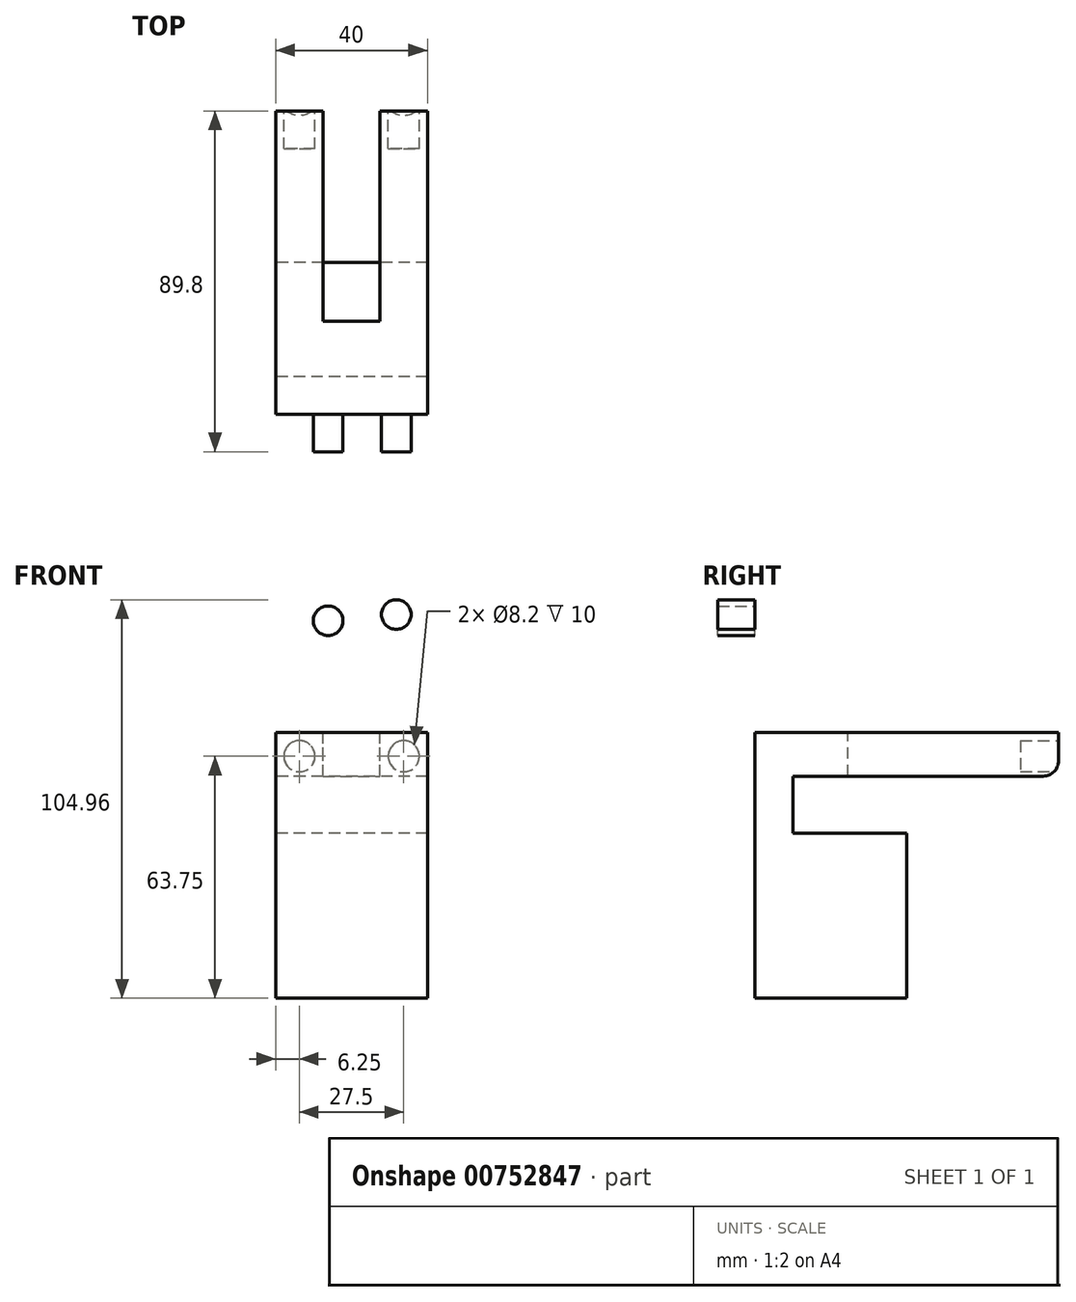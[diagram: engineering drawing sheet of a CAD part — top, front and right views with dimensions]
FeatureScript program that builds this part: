
annotation { "Feature Type Name" : "Feature", "Feature Type Description" : "" }
export const myFeature = defineFeature(function(context is Context, id is Id, definition is map)
    precondition{}
    {
        {
            var Q0;
            Q0=qCreatedBy(makeId("Right.planeOp"),FACE);
            var sketch = newSketch(context, id + "F0", { "sketchPlane" : qUnion([Q0])});
            skLineSegment(sketch, "E0.bottom", {"start": v(0, 0) * mm, "end": v(80, 0) * mm});
            skLineSegment(sketch, "E0.top", {"start": v(0, -40) * mm, "end": v(80, -40) * mm});
            skLineSegment(sketch, "E0.left", {"start": v(0, 0) * mm, "end": v(0, -40) * mm});
            skLineSegment(sketch, "E0.right", {"start": v(80, 0) * mm, "end": v(80, -7.5) * mm});
            skLineSegment(sketch, "E1.bottom", {"start": v(10, -11.5) * mm, "end": v(76, -11.5) * mm});
            skLineSegment(sketch, "E1.top", {"start": v(10, -26.5) * mm, "end": v(80, -26.5) * mm});
            skLineSegment(sketch, "E1.left", {"start": v(10, -11.5) * mm, "end": v(10, -26.5) * mm});
            skLineSegment(sketch, "E1.right", {"start": v(80, -12.5) * mm, "end": v(80, -26.5) * mm});
            skLineSegment(sketch, "E2", {"start": v(40, -40) * mm, "end": v(40, -26.5) * mm});
            skPoint(sketch, "E3.newPointB", {"position": v(80, -40) * mm});
            skArc(sketch, "E3.filletArc", {"start": v(76, -11.5) * mm, "mid": v(78.83, -10.33) * mm, "end": v(80, -7.5) * mm});
            skSolve(sketch);
        }
        {
            var Q0;
            {var subQ1=sQuery(id+"F0.wireOp",EDGE,"E0.bottom");Q0=makeQuery(id+"F0.imprint","IMPRINT",FACE,{"disambiguationData":[TD([[makeQuery(id+"F0.imprint","IMPRINT",EDGE,{"derivedFrom":subQ1}),-1.0]])]});}
            extrude(context, id + "F1", {"entities" : qUnion([Q0]), "depth" : 40 * mm, "offsetDistance" : 25 * mm});
        }
        {
            var Q0;
            Q0=makeQuery(id+"F1.opExtrude","SWEPT_FACE",FACE,{"disambiguationData":[OSD([sQuery(id+"F0.wireOp",EDGE,"E0.bottom")])]});
            var sketch = newSketch(context, id + "F2", { "sketchPlane" : qUnion([Q0])});
            skCircle(sketch, "E4.cCircle", {"center": v(20, 54.76) * mm, "radius": 6.5 * mm, "construction": true});
            skLineSegment(sketch, "E4.0", {"start": v(24, 48.4) * mm, "end": v(16.5, 48.12) * mm});
            skLineSegment(sketch, "E4.1", {"start": v(16.5, 48.12) * mm, "end": v(12.5, 54.47) * mm});
            skLineSegment(sketch, "E4.2", {"start": v(12.5, 54.47) * mm, "end": v(16, 61.1) * mm});
            skLineSegment(sketch, "E4.3", {"start": v(16, 61.1) * mm, "end": v(23.5, 61.4) * mm});
            skLineSegment(sketch, "E4.4", {"start": v(23.5, 61.4) * mm, "end": v(27.5, 55.04) * mm});
            skLineSegment(sketch, "E4.5", {"start": v(27.5, 55.04) * mm, "end": v(24, 48.4) * mm});
            skPoint(sketch, "E4.0.midPoint", {"position": v(20.25, 48.26) * mm});
            skPoint(sketch, "E5.endSnap0", {"position": v(27.96, 47.74) * mm});
            skLineSegment(sketch, "E6", {"start": v(12.5, 24.53) * mm, "end": v(27.5, 24.53) * mm});
            skLineSegment(sketch, "E7", {"start": v(12.5, 54.47) * mm, "end": v(12.5, 24.53) * mm});
            skLineSegment(sketch, "E8", {"start": v(27.5, 55.04) * mm, "end": v(27.5, 24.53) * mm});
            skLineSegment(sketch, "E9", {"start": v(12.5, 54.47) * mm, "end": v(12.5, 80) * mm});
            skLineSegment(sketch, "E10", {"start": v(27.5, 55.04) * mm, "end": v(27.5, 80) * mm});
            skLineSegment(sketch, "E11", {"start": v(40, 80) * mm, "end": v(40, 0) * mm});
            skSolve(sketch);
        }
        {
            var Q0;
            Q0=makeQuery(id+"F2.imprint","IMPRINT",FACE,{"disambiguationData":[TD([[makeQuery(id+"F2.imprint","IMPRINT",EDGE,{"derivedFrom":sQuery(id+"F2.wireOp",EDGE,"E4.2")}),1.0]])]});
            var Q1;
            Q1=makeQuery(id+"F2.imprint","IMPRINT",FACE,{"disambiguationData":[TD([[makeQuery(id+"F2.imprint","IMPRINT",EDGE,{"derivedFrom":sQuery(id+"F2.wireOp",EDGE,"E4.0")}),-1.0]])]});
            var Q2;
            Q2=makeQuery(id+"F2.imprint","IMPRINT",FACE,{"disambiguationData":[TD([[makeQuery(id+"F2.imprint","IMPRINT",EDGE,{"derivedFrom":sQuery(id+"F2.wireOp",EDGE,"E4.0")}),1.0]])]});
            extrude(context, id + "F3", {"entities" : qUnion([Q0, Q1, Q2]), "operationType" : NewBodyOperationType.REMOVE, "oppositeDirection" : true, "depth" : 13 * mm, "offsetDistance" : 25 * mm});
        }
        {
            var Q0;
            Q0=makeQuery(id+"F1.opExtrude","SWEPT_FACE",FACE,{"disambiguationData":[OSD([sQuery(id+"F0.wireOp",EDGE,"E0.top")])]});
            extrude(context, id + "F4", {"entities" : qUnion([Q0]), "operationType" : NewBodyOperationType.ADD, "depth" : 30 * mm, "offsetDistance" : 25 * mm});
        }
        {
            var Q0;
            {var subQ2=sQuery(id+"F0.wireOp",EDGE,"E0.right");Q0=makeQuery(id+"F3.boolean.opBoolean","SPLIT",FACE,{"disambiguationData":[TD([makeQuery(id+"F3.opExtrude","SWEPT_FACE",FACE,{"disambiguationData":[OSD([sQuery(id+"F2.wireOp",EDGE,"E7"),sQuery(id+"F2.wireOp",EDGE,"E9")])]})])],"derivedFrom":makeQuery(id+"F1.opExtrude","SWEPT_FACE",FACE,{"disambiguationData":[OSD([subQ2])]})});}
            var sketch = newSketch(context, id + "F5", { "sketchPlane" : qUnion([Q0])});
            skCircle(sketch, "E12", {"center": v(-33.75, -6.25) * mm, "radius": 4.1 * mm});
            skCircle(sketch, "E13", {"center": v(-6.25, -6.25) * mm, "radius": 4.1 * mm});
            skSolve(sketch);
        }
        {
            var Q0;
            Q0=makeQuery(id+"F5.imprint","IMPRINT",FACE,{"disambiguationData":[TD([[makeQuery(id+"F5.imprint","IMPRINT",EDGE,{"derivedFrom":sQuery(id+"F5.wireOp",EDGE,"E12")}),1.0]])]});
            var Q1;
            Q1=makeQuery(id+"F5.imprint","IMPRINT",FACE,{"disambiguationData":[TD([[makeQuery(id+"F5.imprint","IMPRINT",EDGE,{"derivedFrom":sQuery(id+"F5.wireOp",EDGE,"E13")}),1.0]])]});
            extrude(context, id + "F6", {"entities" : qUnion([Q0, Q1]), "operationType" : NewBodyOperationType.REMOVE, "oppositeDirection" : true, "depth" : 10 * mm, "offsetDistance" : 25 * mm});
        }
        {
            var Q0;
            Q0=qCreatedBy(makeId("Front.planeOp"),FACE);
            var sketch = newSketch(context, id + "F7", { "sketchPlane" : qUnion([Q0])});
            skCircle(sketch, "E14", {"center": v(31.79, 31.06) * mm, "radius": 3.9 * mm});
            skCircle(sketch, "E15", {"center": v(13.83, 29.43) * mm, "radius": 3.9 * mm});
            skSolve(sketch);
        }
        {
            var Q0;
            Q0=makeQuery(id+"F7.imprint","IMPRINT",FACE,{"disambiguationData":[TD([[makeQuery(id+"F7.imprint","IMPRINT",EDGE,{"derivedFrom":sQuery(id+"F7.wireOp",EDGE,"E14")}),1.0]])]});
            var Q1;
            Q1=makeQuery(id+"F7.imprint","IMPRINT",FACE,{"disambiguationData":[TD([[makeQuery(id+"F7.imprint","IMPRINT",EDGE,{"derivedFrom":sQuery(id+"F7.wireOp",EDGE,"E15")}),1.0]])]});
            extrude(context, id + "F8", {"entities" : qUnion([Q0, Q1]), "depth" : 9.8 * mm, "offsetDistance" : 25 * mm});
        }
    });
